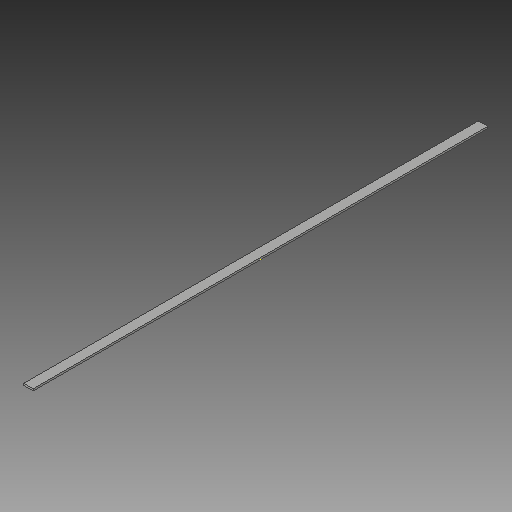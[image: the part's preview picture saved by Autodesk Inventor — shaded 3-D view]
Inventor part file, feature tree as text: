
AUTODESK INVENTOR PART (.ipt)
format: ipt  version: 2018 (Build 220112000, 112)  size: 80,384 bytes
history: native  units: mm
features: extrude x1, other x1, sketch x1
ambient origin geometry x8: Origin, YZ Plane, XZ Plane, XY Plane, X Axis, Y Axis, Z Axis, Center Point
bodies: Solid1 (feature_tree)
feature tree (3):
  extrude  "Extrusion1"  Depth=5.0mm
  other  "Work Axis1"
  sketch  "Sketch1"  dims[d0=25.0mm d1=5.0mm d2=1208.95mm d3=0.0mm]
